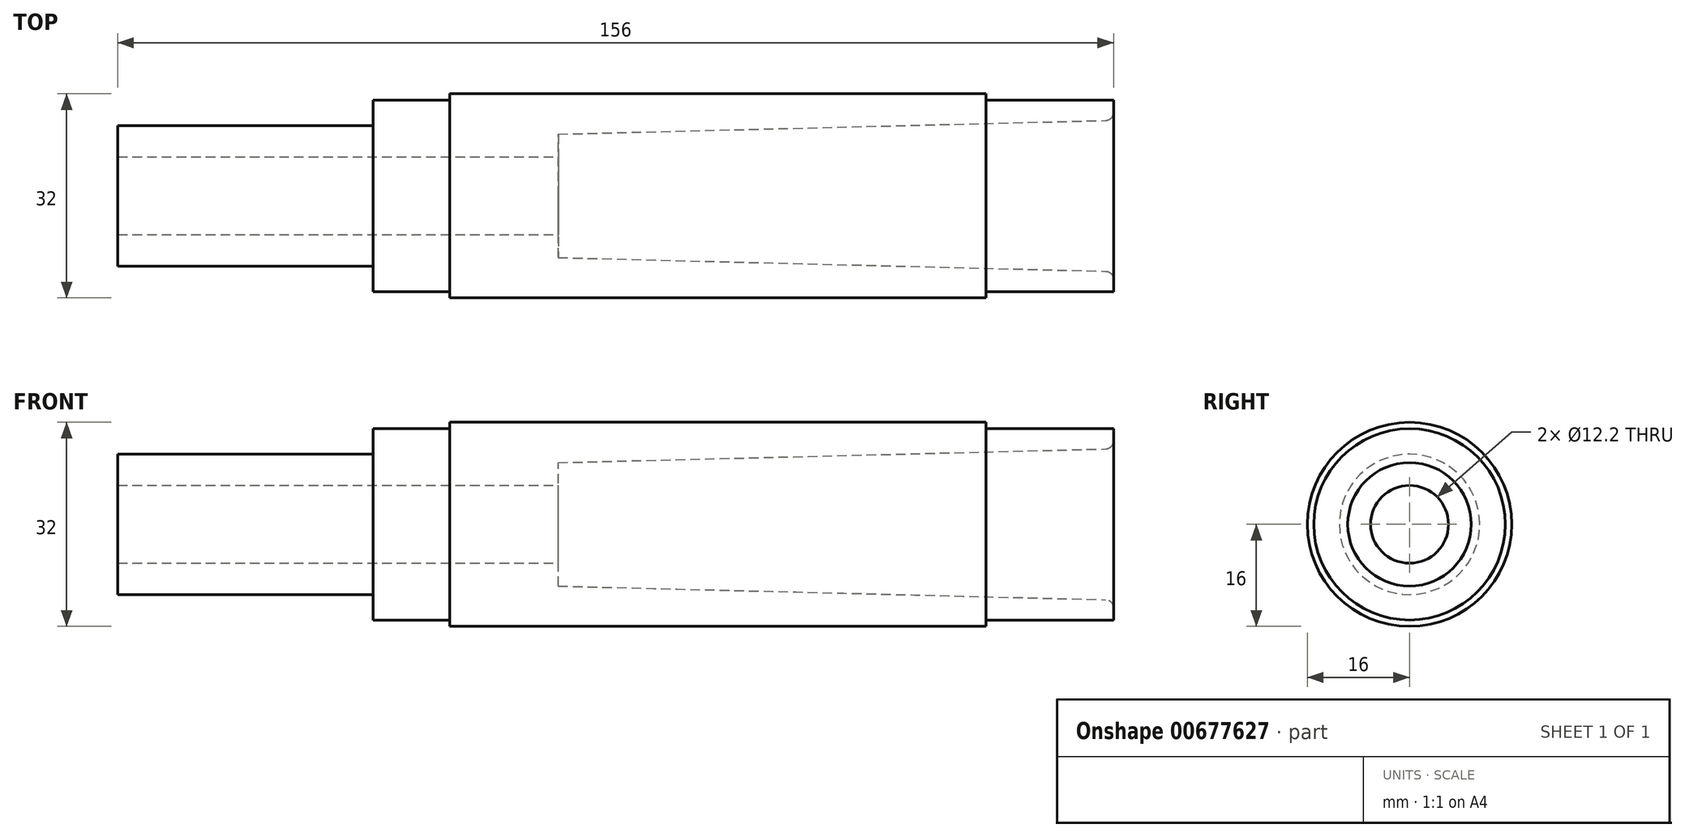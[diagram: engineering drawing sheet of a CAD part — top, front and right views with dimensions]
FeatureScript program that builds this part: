
annotation { "Feature Type Name" : "Feature", "Feature Type Description" : "" }
export const myFeature = defineFeature(function(context is Context, id is Id, definition is map)
    precondition{}
    {
        {
            var Q0;
            Q0=qCreatedBy(makeId("Top.planeOp"),FACE);
            var sketch = newSketch(context, id + "F0", { "sketchPlane" : qUnion([Q0])});
            skLineSegment(sketch, "E0.bottom", {"start": v(33, 15) * mm, "end": v(53, 15) * mm});
            skLineSegment(sketch, "E0.top", {"start": v(33, -15) * mm, "end": v(53, -15) * mm});
            skLineSegment(sketch, "E0.left", {"start": v(-63, 15) * mm, "end": v(-63, 11) * mm});
            skLineSegment(sketch, "E0.right", {"start": v(53, 15) * mm, "end": v(53, -15) * mm});
            skLineSegment(sketch, "E1.bottom", {"start": v(-103, 11) * mm, "end": v(-63, 11) * mm});
            skLineSegment(sketch, "E1.top", {"start": v(-103, -11) * mm, "end": v(-63, -11) * mm});
            skLineSegment(sketch, "E1.left", {"start": v(-103, 11) * mm, "end": v(-103, -11) * mm});
            skLineSegment(sketch, "E2.bottom", {"start": v(-51, -16) * mm, "end": v(33, -16) * mm});
            skLineSegment(sketch, "E2.top", {"start": v(-51, 16) * mm, "end": v(33, 16) * mm});
            skLineSegment(sketch, "E2.right", {"start": v(33, -16) * mm, "end": v(33, -15) * mm});
            skLineSegment(sketch, "E3", {"start": v(0, 0) * mm, "end": v(-103, 0) * mm});
            skLineSegment(sketch, "E4", {"start": v(53, 0) * mm, "end": v(0, 0) * mm});
            skLineSegment(sketch, "E5", {"start": v(0, 0) * mm, "end": v(33, 0) * mm});
            skLineSegment(sketch, "E6.trimOffspring", {"start": v(33, 15) * mm, "end": v(33, 16) * mm});
            skLineSegment(sketch, "E7.trimOffspring", {"start": v(-63, 11) * mm, "end": v(-63, 15) * mm});
            skLineSegment(sketch, "E8", {"start": v(-51, 16) * mm, "end": v(-51, -16) * mm});
            skLineSegment(sketch, "E9", {"start": v(-51, -15) * mm, "end": v(-63, -15) * mm});
            skPoint(sketch, "E9.endSnap0", {"position": v(-63, -13) * mm});
            skLineSegment(sketch, "E10", {"start": v(-51, 15) * mm, "end": v(-63, 15) * mm});
            skPoint(sketch, "E11.trimOffspring.start.orphan", {"position": v(-63, -15) * mm});
            skLineSegment(sketch, "E12", {"start": v(-63, -15) * mm, "end": v(-63, -11) * mm});
            skSolve(sketch);
        }
        {
            var Q0;
            {var subQ6=sQuery(id+"F0.wireOp",EDGE,"E0.top");Q0=makeQuery(id+"F0.imprint","IMPRINT",FACE,{"disambiguationData":[TD([[makeQuery(id+"F0.imprint","IMPRINT",EDGE,{"derivedFrom":subQ6}),1.0]])]});}
            var Q1;
            {var subQ6=sQuery(id+"F0.wireOp",EDGE,"E1.top");Q1=makeQuery(id+"F0.imprint","IMPRINT",FACE,{"disambiguationData":[TD([[makeQuery(id+"F0.imprint","IMPRINT",EDGE,{"derivedFrom":subQ6}),1.0]])]});}
            var Q2;
            Q2=sQuery(id+"F0.wireOp",EDGE,"E3");
            revolve(context, id + "F1", {"entities" : qUnion([Q0, Q1]), "axis" : qUnion([Q2]), "revolveType" : RevolveType.FULL});
        }
        {
            var Q0;
            Q0=qCreatedBy(makeId("Front.planeOp"),FACE);
            var sketch = newSketch(context, id + "F2", { "sketchPlane" : qUnion([Q0])});
            skLineSegment(sketch, "E13", {"start": v(-34, 9.68) * mm, "end": v(-34, -9.68) * mm});
            skLineSegment(sketch, "E14", {"start": v(-34, 9.68) * mm, "end": v(53, 11.85) * mm});
            skLineSegment(sketch, "E15", {"start": v(53, 11.85) * mm, "end": v(53, -11.85) * mm});
            skLineSegment(sketch, "E16", {"start": v(53, -11.85) * mm, "end": v(-34, -9.68) * mm});
            skLineSegment(sketch, "E17", {"start": v(0, 0) * mm, "end": v(-34, 0) * mm});
            skLineSegment(sketch, "E18", {"start": v(53, 0) * mm, "end": v(0, 0) * mm});
            skLineSegment(sketch, "E19.bottom", {"start": v(-134, 6.1) * mm, "end": v(-34, 6.1) * mm});
            skLineSegment(sketch, "E19.top", {"start": v(-134, -6.1) * mm, "end": v(-34, -6.1) * mm});
            skLineSegment(sketch, "E19.left", {"start": v(-134, 6.1) * mm, "end": v(-134, -6.1) * mm});
            skLineSegment(sketch, "E19.right", {"start": v(-34, 6.1) * mm, "end": v(-34, -6.1) * mm});
            skLineSegment(sketch, "E20", {"start": v(-134, 0) * mm, "end": v(-34, 0) * mm});
            skSolve(sketch);
        }
        {
            var Q0;
            {var subQ2=sQuery(id+"F2.wireOp",EDGE,"E14");Q0=makeQuery(id+"F2.imprint","IMPRINT",FACE,{"disambiguationData":[TD([[makeQuery(id+"F2.imprint","IMPRINT",EDGE,{"derivedFrom":subQ2}),-1.0]])]});}
            var Q1;
            {var subQ0=sQuery(id+"F2.wireOp",EDGE,"E19.bottom");Q1=makeQuery(id+"F2.imprint","IMPRINT",FACE,{"disambiguationData":[TD([[makeQuery(id+"F2.imprint","IMPRINT",EDGE,{"derivedFrom":subQ0}),-1.0]])]});}
            var Q2;
            Q2=sQuery(id+"F0.wireOp",EDGE,"E4");
            revolve(context, id + "F3", {"operationType" : NewBodyOperationType.REMOVE, "entities" : qUnion([Q0, Q1]), "axis" : qUnion([Q2]), "revolveType" : RevolveType.FULL});
        }
        {
            var Q0;
            Q0=makeQuery(id+"F3.boolean.opBoolean","INTERSECT",EDGE,{"derivedFrom":[makeQuery(id+"F1.opRevolve","SWEPT_FACE",FACE,{"disambiguationData":[OSD([sQuery(id+"F0.wireOp",EDGE,"E0.right")])]}),makeQuery(id+"F3.opRevolve","SWEPT_FACE",FACE,{"disambiguationData":[OSD([sQuery(id+"F2.wireOp",EDGE,"E14")])]})]});
            fillet(context, id + "F4", {"entities" : qUnion([Q0]), "radius" : 1.3 * mm, "tangentPropagation" : true, "allowEdgeOverflow" : false});
        }
        {
            var Q0;
            Q0=makeQuery(id+"F1.opRevolve","SWEPT_BODY",BODY,{"disambiguationData":[OSD([sQuery(id+"F0.wireOp",EDGE,"E0.top"),sQuery(id+"F0.wireOp",EDGE,"E0.right"),sQuery(id+"F0.wireOp",EDGE,"E1.top"),sQuery(id+"F0.wireOp",EDGE,"E1.left"),sQuery(id+"F0.wireOp",EDGE,"E2.bottom"),sQuery(id+"F0.wireOp",EDGE,"E2.right"),sQuery(id+"F0.wireOp",EDGE,"E3"),sQuery(id+"F0.wireOp",EDGE,"E4"),sQuery(id+"F0.wireOp",EDGE,"E5"),sQuery(id+"F0.wireOp",EDGE,"E8"),sQuery(id+"F0.wireOp",EDGE,"E9"),sQuery(id+"F0.wireOp",EDGE,"E12")])]});
            transform(context, id + "F5", {"entities" : qUnion([Q0]), "transformType" : TransformType.TRANSLATION_3D, "dx" : 0 * mm, "dy" : 0 * mm, "dz" : 0 * mm, "makeCopy" : true});
        }
    });
